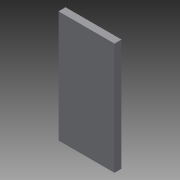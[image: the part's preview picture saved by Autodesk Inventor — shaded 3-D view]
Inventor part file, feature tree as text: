
AUTODESK INVENTOR PART (.ipt)
format: ipt  version: 2016 (Build 200138000, 138)  size: 69,120 bytes
history: native  units: in
note: dims shown in document units (in); Inventor stores cm internally (conversion verified against a paired STEP export)
features: extrude x1, sketch x1
ambient origin geometry x8: Origin, YZ Plane, XZ Plane, XY Plane, X Axis, Y Axis, Z Axis, Center Point
bodies: Solid1 (feature_tree)
feature tree (2):
  extrude  "Extrusion1"  Depth=2.0in
  sketch  "Sketch1"  dims[d0=1.0in d1=2.0in d2=0.125in d3=0.0in]
